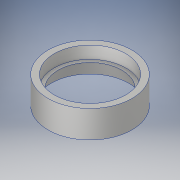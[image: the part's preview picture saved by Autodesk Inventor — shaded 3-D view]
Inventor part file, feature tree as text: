
AUTODESK INVENTOR PART (.ipt)
format: ipt  version: 2017 (Build 210142000, 142)  size: 143,360 bytes
history: native  units: in
note: dims shown in document units (in); Inventor stores cm internally (conversion verified against a paired STEP export)
features: revolve x1, sketch x1
ambient origin geometry x8: Origin, YZ Plane, XZ Plane, XY Plane, X Axis, Y Axis, Z Axis, Center Point
bodies: Body1 (feature_tree)
feature tree (2):
  revolve  "Revolution3"  [1 undecoded]
  sketch  "Sketch1"  dims[d0=0.25in d1=0.1718in d2=15.0deg d4=0.25in d5=1.5in d6=1.25in d7=0.25in d11=0.25in d13=0.5in d15=0.25in d16=0.25in d18=0.125in d19=0.5in d20=0.125in d21=0.25in d22=0.125in d23=0.125in d24=0.25in d25=0.5in d26=2.292in d27=0.5in d29=0.5in d31=90.0deg]
note: 1 required parameter value undecoded (feature->parameter linkage not recoverable at this tier; creation-order binding heuristic only, values carry confidence <= 0.55)
